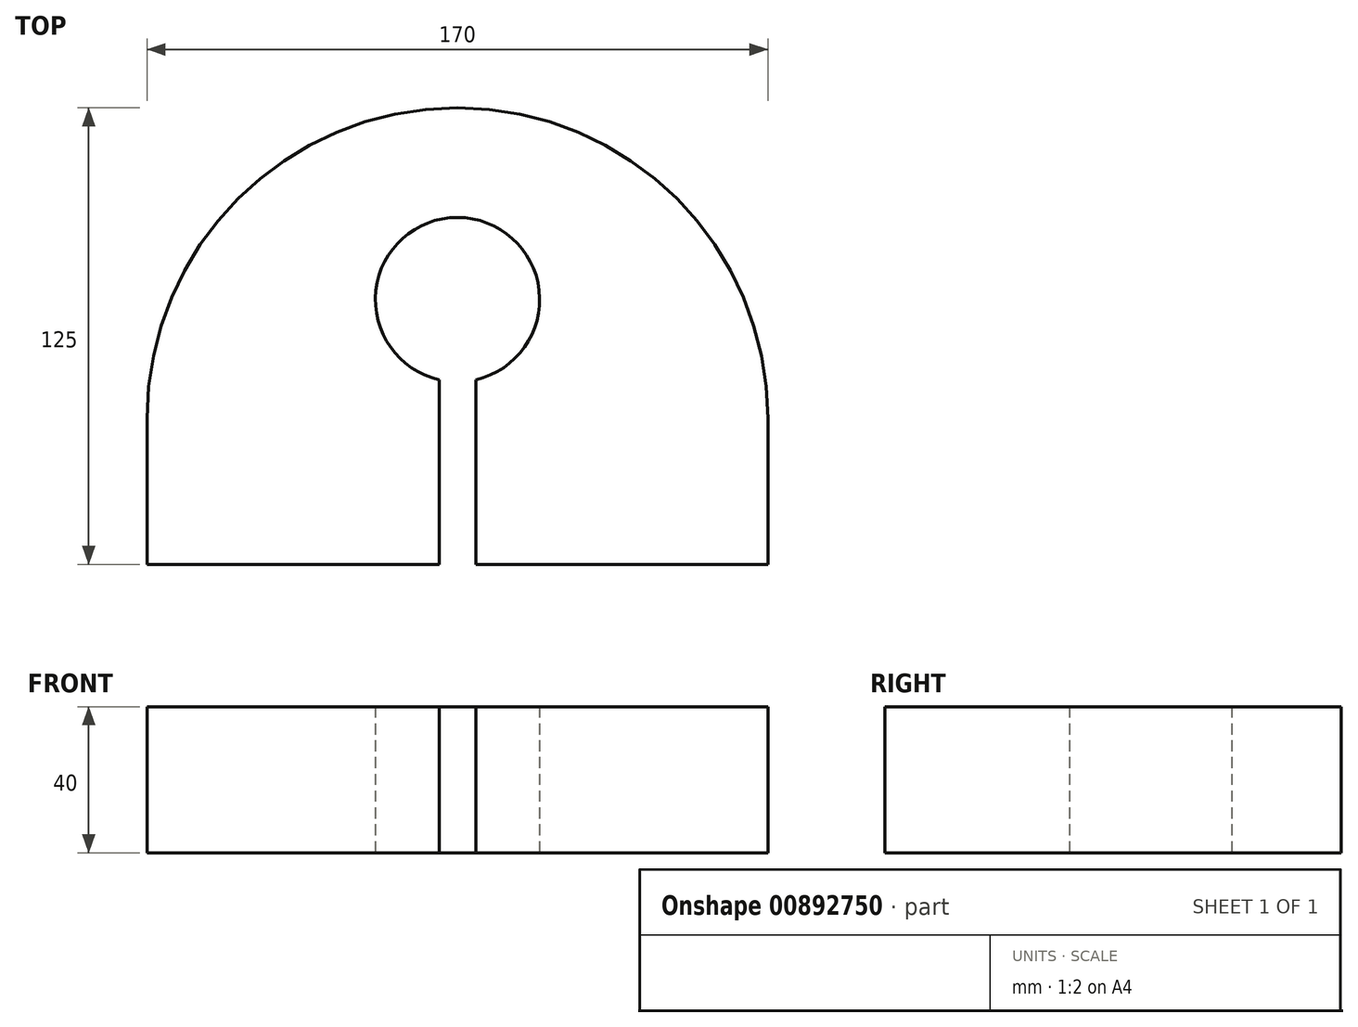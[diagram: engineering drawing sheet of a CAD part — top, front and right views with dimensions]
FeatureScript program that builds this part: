
annotation { "Feature Type Name" : "Feature", "Feature Type Description" : "" }
export const myFeature = defineFeature(function(context is Context, id is Id, definition is map)
    precondition{}
    {
        {
            var Q0;
            Q0=qCreatedBy(makeId("Top.planeOp"),FACE);
            var sketch = newSketch(context, id + "F0", { "sketchPlane" : qUnion([Q0])});
            skLineSegment(sketch, "E0.bottom", {"start": v(-85, 125) * mm, "end": v(-85, 125) * mm});
            skLineSegment(sketch, "E0.top", {"start": v(-170, 0) * mm, "end": v(-85, 0) * mm});
            skLineSegment(sketch, "E0.left", {"start": v(-170, 40) * mm, "end": v(-170, 0) * mm});
            skLineSegment(sketch, "E0.right", {"start": v(0, 40) * mm, "end": v(0, 0) * mm});
            skArc(sketch, "E1", {"start": v(-80, 50.56) * mm, "mid": v(-85, 95) * mm, "end": v(-90, 50.56) * mm});
            skPoint(sketch, "E1.centerSnap0", {"position": v(-85, 0) * mm});
            skPoint(sketch, "E2", {"position": v(-170, 25) * mm});
            skPoint(sketch, "E3", {"position": v(0, 25) * mm});
            skPoint(sketch, "E4.visualSharp", {"position": v(-170, 125) * mm});
            skArc(sketch, "E4.filletArc", {"start": v(-85, 125) * mm, "mid": v(-145.1, 100.1) * mm, "end": v(-170, 40) * mm});
            skPoint(sketch, "E5.visualSharp", {"position": v(0, 125) * mm});
            skArc(sketch, "E5.filletArc", {"start": v(0, 40) * mm, "mid": v(-24.9, 100.1) * mm, "end": v(-85, 125) * mm});
            skLineSegment(sketch, "E6", {"start": v(-90, 0) * mm, "end": v(-90, 50.56) * mm});
            skLineSegment(sketch, "E7", {"start": v(-80, 0) * mm, "end": v(-80, 50.56) * mm});
            skLineSegment(sketch, "E8.trimOffspring", {"start": v(-80, 0) * mm, "end": v(0, 0) * mm});
            skSolve(sketch);
        }
        {
            var Q0;
            Q0 = qSketchRegion(id + "F0", true);
            extrude(context, id + "F1", {"entities" : qUnion([Q0]), "depth" : 40 * mm, "offsetDistance" : 25 * mm});
        }
    });
